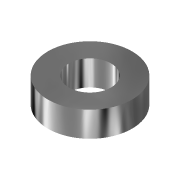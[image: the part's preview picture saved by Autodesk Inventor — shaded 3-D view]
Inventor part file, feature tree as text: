
AUTODESK INVENTOR PART (.ipt)
format: ipt  version: 2022 (Build 260153000, 153)  size: 88,576 bytes
history: native  units: mm
features: extrude x1, sketch x1
ambient origin geometry x8: Origin, YZ Plane, XZ Plane, XY Plane, X Axis, Y Axis, Z Axis, Center Point
bodies: Volumenkörper1 (feature_tree)
feature tree (2):
  extrude  "Extrusion1"  Depth=5.0mm
  sketch  "Skizze1"  dims[d0=10.0mm d1=5.0mm d2=3.0mm d3=0.0mm]
